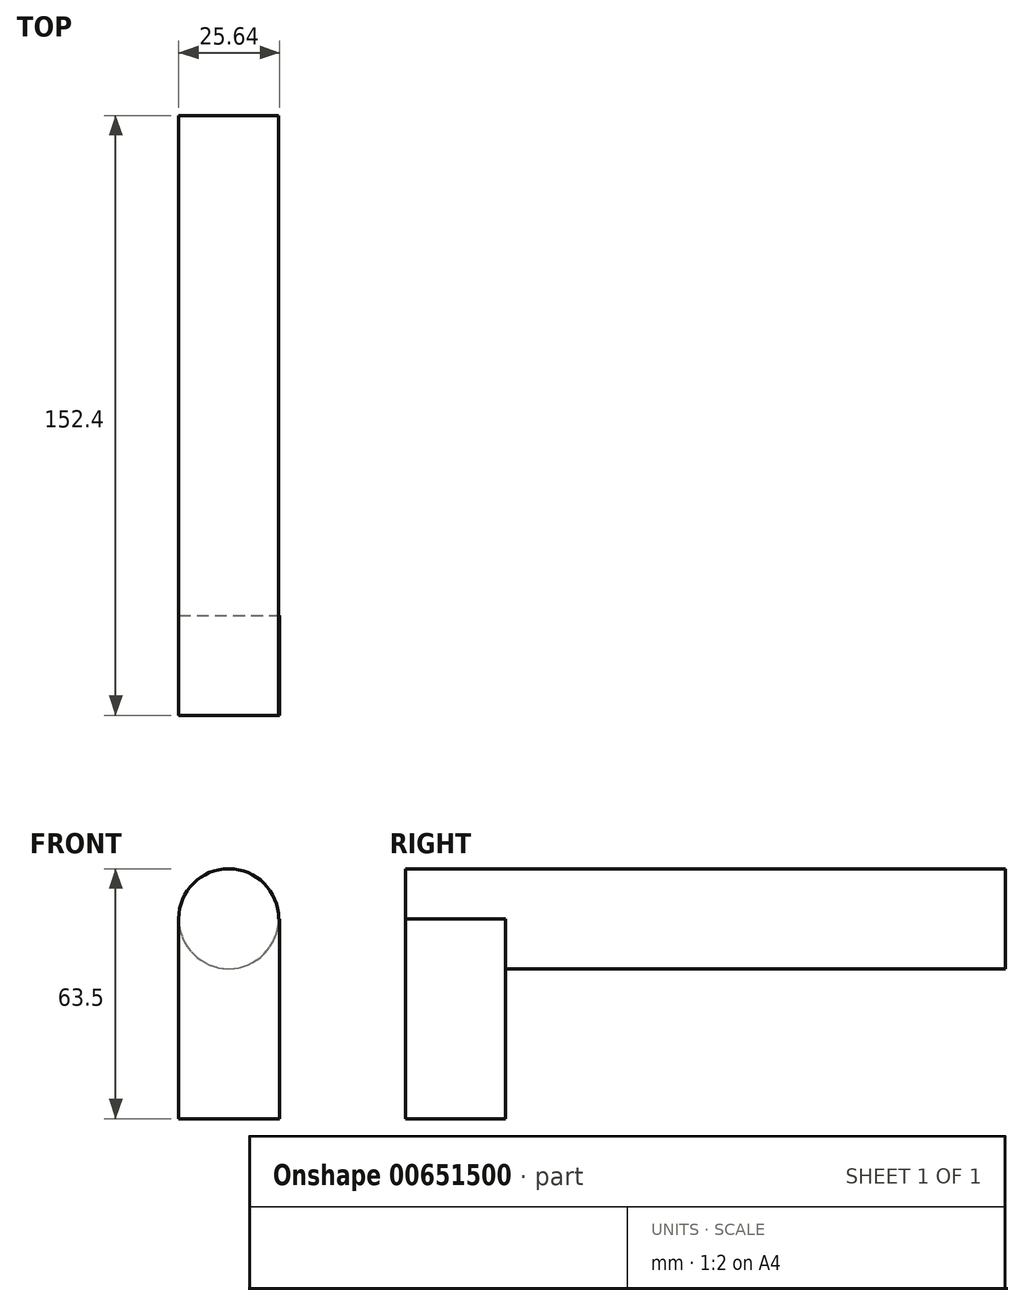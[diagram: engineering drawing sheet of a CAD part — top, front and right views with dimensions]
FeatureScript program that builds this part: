
annotation { "Feature Type Name" : "Feature", "Feature Type Description" : "" }
export const myFeature = defineFeature(function(context is Context, id is Id, definition is map)
    precondition{}
    {
        {
            var Q0;
            Q0=qCreatedBy(makeId("Front.planeOp"),FACE);
            var sketch = newSketch(context, id + "F0", { "sketchPlane" : qUnion([Q0])});
            skCircle(sketch, "E0", {"center": v(-27.74, 61.12) * mm, "radius": 12.7 * mm});
            skSolve(sketch);
        }
        {
            var Q0;
            Q0=makeQuery(id+"F0.imprint","IMPRINT",FACE,{"disambiguationData":[TD([[makeQuery(id+"F0.imprint","IMPRINT",EDGE,{"derivedFrom":sQuery(id+"F0.wireOp",EDGE,"E0")}),1.0]])]});
            var sketch = newSketch(context, id + "F1", { "sketchPlane" : qUnion([Q0])});
            skSolve(sketch);
        }
        {
            var Q0;
            Q0=makeQuery(id+"F1.imprint","IMPRINT",FACE,{"disambiguationData":[TD([[makeQuery(id+"F1.imprint","IMPRINT",EDGE,{"derivedFrom":makeQuery(id+"F0.imprint","IMPRINT",EDGE,{"derivedFrom":sQuery(id+"F0.wireOp",EDGE,"E0")})}),1.0]])]});
            extrude(context, id + "F2", {"entities" : qUnion([Q0]), "depth" : 152.4 * mm, "offsetDistance" : 25.4 * mm});
        }
        {
            var Q0;
            Q0=makeQuery(id+"F2.opExtrude","CAP_FACE",FACE,{"disambiguationData":[OSD([sQuery(id+"F0.wireOp",EDGE,"E0")])],"isStart":false});
            var sketch = newSketch(context, id + "F3", { "sketchPlane" : qUnion([Q0])});
            skLineSegment(sketch, "E1", {"start": v(-27.74, 61.12) * mm, "end": v(-15.04, 61.12) * mm});
            skLineSegment(sketch, "E2", {"start": v(-15.04, 61.12) * mm, "end": v(-40.44, 61.12) * mm});
            skLineSegment(sketch, "E3.bottom", {"start": v(-40.44, 61.12) * mm, "end": v(-14.8, 61.12) * mm});
            skLineSegment(sketch, "E3.top", {"start": v(-40.44, 10.32) * mm, "end": v(-14.8, 10.32) * mm});
            skLineSegment(sketch, "E3.left", {"start": v(-40.44, 61.12) * mm, "end": v(-40.44, 10.32) * mm});
            skLineSegment(sketch, "E3.right", {"start": v(-14.8, 61.12) * mm, "end": v(-14.8, 10.32) * mm});
            skSolve(sketch);
        }
        {
            var Q0;
            {var subQ0=sQuery(id+"F3.wireOp",EDGE,"E3.bottom");var subQ3=makeQuery(id+"F3.imprint","IMPRINT",VERTEX,{"derivedFrom":subQ0});Q0=makeQuery(id+"F3.imprint","IMPRINT",FACE,{"disambiguationData":[TD([[makeQuery(id+"F3.imprint","IMPRINT",EDGE,{"disambiguationData":[TD([[subQ3,-1.0]])],"derivedFrom":subQ0}),-1.0]])]});}
            var Q1;
            Q1=makeQuery(id+"F3.imprint","IMPRINT",FACE,{"disambiguationData":[TD([[makeQuery(id+"F3.imprint","IMPRINT",EDGE,{"derivedFrom":sQuery(id+"F3.wireOp",EDGE,"E3.top")}),1.0]])]});
            extrude(context, id + "F4", {"entities" : qUnion([Q0, Q1]), "operationType" : NewBodyOperationType.ADD, "depth" : -25.4 * mm, "offsetDistance" : 25.4 * mm});
        }
    });
